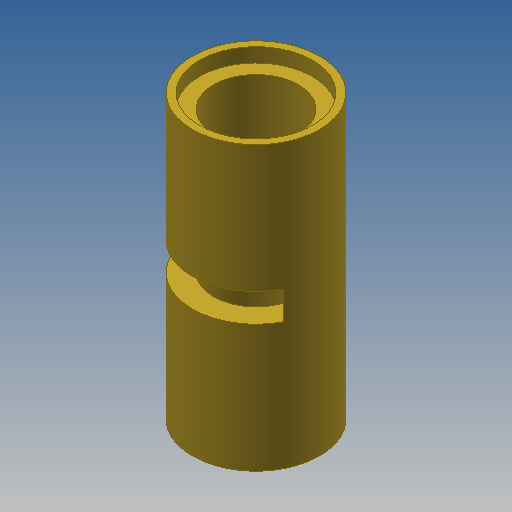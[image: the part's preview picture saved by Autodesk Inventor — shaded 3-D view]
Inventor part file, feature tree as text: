
AUTODESK INVENTOR PART (.ipt)
format: ipt  version: 2022.2 (Build 262287000, 287)  size: 132,608 bytes
history: native  units: in
note: dims shown in document units (in); Inventor stores cm internally (conversion verified against a paired STEP export)
features: sketch x2, revolve x1, extrude x1
ambient origin geometry x8: Origin, YZ Plane, XZ Plane, XY Plane, X Axis, Y Axis, Z Axis, Center Point
bodies: Solid1 (feature_tree)
feature tree (4):
  revolve  "Revolution1"  [1 undecoded]
  extrude  "Extrusion1"  Depth=0.3937in
  sketch  "Sketch2"  dims[d0=0.6299in d1=0.252in]
  sketch  "Sketch3"  dims[d2=0.2835in d3=0.189in d4=0.0315in d5=0.063in d6=90.0deg d7=0.3937in d8=0.0in]
note: 1 required parameter value undecoded (feature->parameter linkage not recoverable at this tier; creation-order binding heuristic only, values carry confidence <= 0.55)
